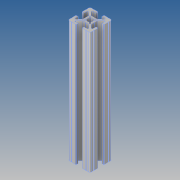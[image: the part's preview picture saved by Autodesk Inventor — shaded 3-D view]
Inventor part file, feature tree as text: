
AUTODESK INVENTOR PART (.ipt)
format: ipt  version: 2018.2 (Build 222227000, 227)  size: 225,792 bytes
history: native  units: mm
features: other x2, extrude x1
ambient origin geometry x8: Origin, YZ Plane, XZ Plane, XY Plane, X Axis, Y Axis, Z Axis, Center Point
bodies: Volumenkörper1 (feature_tree)
feature tree (3):
  other  "90-50-PROFILES-30x30xX.ipt"
  extrude  "Extrusion1"  Depth=10.0mm
  other  "Profil_Skizze"
